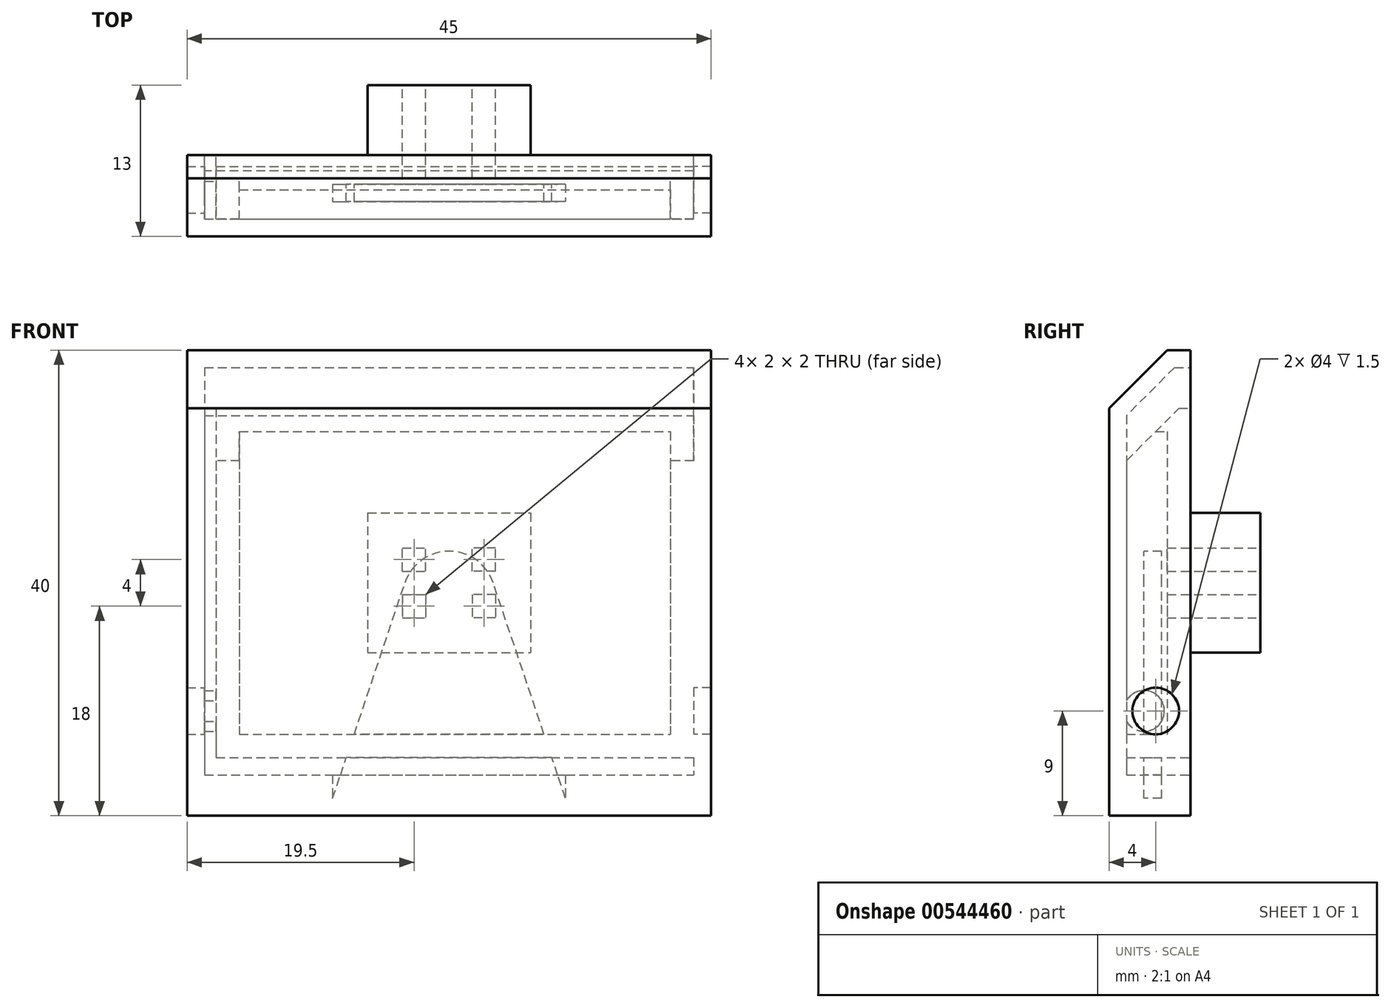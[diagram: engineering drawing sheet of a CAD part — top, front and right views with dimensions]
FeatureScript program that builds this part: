
annotation { "Feature Type Name" : "Feature", "Feature Type Description" : "" }
export const myFeature = defineFeature(function(context is Context, id is Id, definition is map)
    precondition{}
    {
        {
            var Q0;
            Q0=qCreatedBy(makeId("Front.planeOp"),FACE);
            var sketch = newSketch(context, id + "F0", { "sketchPlane" : qUnion([Q0])});
            skLineSegment(sketch, "E0.bottom", {"start": v(-20, 15) * mm, "end": v(21, 15) * mm});
            skLineSegment(sketch, "E0.top", {"start": v(-20, -15) * mm, "end": v(21, -15) * mm});
            skLineSegment(sketch, "E0.left", {"start": v(-20, 15) * mm, "end": v(-20, -15) * mm});
            skLineSegment(sketch, "E0.right", {"start": v(21, 15) * mm, "end": v(21, -15) * mm});
            skSolve(sketch);
        }
        {
            var Q0;
            Q0=makeQuery(id+"F0.imprint","IMPRINT",FACE,{"disambiguationData":[TD([[makeQuery(id+"F0.imprint","IMPRINT",EDGE,{"derivedFrom":sQuery(id+"F0.wireOp",EDGE,"E0.bottom")}),-1.0]])]});
            extrude(context, id + "F1", {"entities" : qUnion([Q0]), "depth" : 6 * mm, "offsetDistance" : 25 * mm});
        }
        {
            var Q0;
            Q0=makeQuery(id+"F1.opExtrude","CAP_FACE",FACE,{"disambiguationData":[OSD([sQuery(id+"F0.wireOp",EDGE,"E0.bottom"),sQuery(id+"F0.wireOp",EDGE,"E0.top"),sQuery(id+"F0.wireOp",EDGE,"E0.left"),sQuery(id+"F0.wireOp",EDGE,"E0.right"),sQuery(id+"F0.wireOp",EDGE,"RBEQEyJk-aGxJ-4fvi-WYVx-bpJPuigMuznj.bottom"),sQuery(id+"F0.wireOp",EDGE,"RBEQEyJk-aGxJ-4fvi-WYVx-bpJPuigMuznj.top"),sQuery(id+"F0.wireOp",EDGE,"RBEQEyJk-aGxJ-4fvi-WYVx-bpJPuigMuznj.left"),sQuery(id+"F0.wireOp",EDGE,"RBEQEyJk-aGxJ-4fvi-WYVx-bpJPuigMuznj.right"),sQuery(id+"F0.wireOp",EDGE,"3556d0db-5f9f-403e-93f9-4f2c554f31b60.MirrorCS"),sQuery(id+"F0.wireOp",EDGE,"3556d0db-5f9f-403e-93f9-4f2c554f31b61.MirrorCS"),sQuery(id+"F0.wireOp",EDGE,"3556d0db-5f9f-403e-93f9-4f2c554f31b62.MirrorCS"),sQuery(id+"F0.wireOp",EDGE,"3556d0db-5f9f-403e-93f9-4f2c554f31b63.MirrorCS"),sQuery(id+"F0.wireOp",EDGE,"c14dda6f-b8be-4261-b637-7746e7f6adf01.MirrorCS"),sQuery(id+"F0.wireOp",EDGE,"c14dda6f-b8be-4261-b637-7746e7f6adf02.MirrorCS"),sQuery(id+"F0.wireOp",EDGE,"c14dda6f-b8be-4261-b637-7746e7f6adf04.MirrorCS"),sQuery(id+"F0.wireOp",EDGE,"c14dda6f-b8be-4261-b637-7746e7f6adf05.MirrorCS"),sQuery(id+"F0.wireOp",EDGE,"c14dda6f-b8be-4261-b637-7746e7f6adf06.MirrorCS"),sQuery(id+"F0.wireOp",EDGE,"c14dda6f-b8be-4261-b637-7746e7f6adf08.MirrorCS"),sQuery(id+"F0.wireOp",EDGE,"c14dda6f-b8be-4261-b637-7746e7f6adf09.MirrorCS"),sQuery(id+"F0.wireOp",EDGE,"c14dda6f-b8be-4261-b637-7746e7f6adf012.MirrorCS")])],"isStart":false});
            shell(context, id + "F2", {"entities" : qUnion([Q0]), "thickness" : 2 * mm});
        }
        {
            var Q0;
            Q0=makeQuery(id+"F0.imprint","IMPRINT",FACE,{"disambiguationData":[TD([[makeQuery(id+"F0.imprint","IMPRINT",EDGE,{"derivedFrom":sQuery(id+"F0.wireOp",EDGE,"E0.bottom")}),-1.0]])]});
            var sketch = newSketch(context, id + "F3", { "sketchPlane" : qUnion([Q0])});
            skLineSegment(sketch, "E1.bottom", {"start": v(-3, -2) * mm, "end": v(3, -2) * mm, "construction": true});
            skLineSegment(sketch, "E1.top", {"start": v(-3, 2) * mm, "end": v(3, 2) * mm, "construction": true});
            skLineSegment(sketch, "E1.left", {"start": v(-3, -2) * mm, "end": v(-3, 2) * mm, "construction": true});
            skLineSegment(sketch, "E1.right", {"start": v(3, -2) * mm, "end": v(3, 2) * mm, "construction": true});
            skPoint(sketch, "E1.middle", {"position": v(0, 0) * mm});
            skLineSegment(sketch, "E2.bottom", {"start": v(-2, -3) * mm, "end": v(-4, -3) * mm});
            skLineSegment(sketch, "E2.top", {"start": v(-2, -1) * mm, "end": v(-4, -1) * mm});
            skLineSegment(sketch, "E2.left", {"start": v(-2, -3) * mm, "end": v(-2, -1) * mm});
            skLineSegment(sketch, "E2.right", {"start": v(-4, -3) * mm, "end": v(-4, -1) * mm});
            skPoint(sketch, "E2.middle", {"position": v(-3, -2) * mm});
            skLineSegment(sketch, "E3.MirrorCS", {"start": v(4, -3) * mm, "end": v(4, -1) * mm});
            skLineSegment(sketch, "E4.MirrorCS", {"start": v(2, -1) * mm, "end": v(4, -1) * mm});
            skLineSegment(sketch, "E5.MirrorCS", {"start": v(2, -3) * mm, "end": v(2, -1) * mm});
            skLineSegment(sketch, "E6.MirrorCS", {"start": v(2, -3) * mm, "end": v(4, -3) * mm});
            skPoint(sketch, "E7.MirrorP", {"position": v(3, -2) * mm});
            skLineSegment(sketch, "E8.MirrorCS", {"start": v(2, 3) * mm, "end": v(2, 1) * mm});
            skLineSegment(sketch, "E9.MirrorCS", {"start": v(2, 1) * mm, "end": v(4, 1) * mm});
            skPoint(sketch, "E10.MirrorP", {"position": v(-3, 2) * mm});
            skLineSegment(sketch, "E11.MirrorCS", {"start": v(-4, 3) * mm, "end": v(-4, 1) * mm});
            skLineSegment(sketch, "E12.MirrorCS", {"start": v(4, 3) * mm, "end": v(4, 1) * mm});
            skLineSegment(sketch, "E13.MirrorCS", {"start": v(2, 3) * mm, "end": v(4, 3) * mm});
            skLineSegment(sketch, "E14.MirrorCS", {"start": v(-2, 3) * mm, "end": v(-2, 1) * mm});
            skLineSegment(sketch, "E15.MirrorCS", {"start": v(-2, 1) * mm, "end": v(-4, 1) * mm});
            skPoint(sketch, "E16.MirrorP", {"position": v(3, 2) * mm});
            skLineSegment(sketch, "E17.MirrorCS", {"start": v(-2, 3) * mm, "end": v(-4, 3) * mm});
            skSolve(sketch);
        }
        {
            var Q0;
            Q0=qSketchRegion(id+"F3",true);
            extrude(context, id + "F4", {"entities" : qUnion([Q0]), "operationType" : NewBodyOperationType.REMOVE, "depth" : 10 * mm, "offsetDistance" : 25 * mm});
        }
        {
            var Q0;
            Q0=makeQuery(id+"F1.opExtrude","SWEPT_FACE",FACE,{"disambiguationData":[OSD([sQuery(id+"F0.wireOp",EDGE,"E0.right")])]});
            var sketch = newSketch(context, id + "F5", { "sketchPlane" : qUnion([Q0])});
            skCircle(sketch, "E18", {"center": v(-4, -11) * mm, "radius": 1.75 * mm});
            skSolve(sketch);
        }
        {
            var Q0;
            Q0=qSketchRegion(id+"F5",true);
            extrude(context, id + "F6", {"entities" : qUnion([Q0]), "operationType" : NewBodyOperationType.ADD, "depth" : 1 * mm, "offsetDistance" : 25 * mm});
        }
        {
            var Q0;
            Q0=makeQuery(id+"F1.opExtrude","SWEPT_FACE",FACE,{"disambiguationData":[OSD([sQuery(id+"F0.wireOp",EDGE,"E0.left")])]});
            var sketch = newSketch(context, id + "F7", { "sketchPlane" : qUnion([Q0])});
            skCircle(sketch, "E19", {"center": v(4, -11) * mm, "radius": 1.75 * mm});
            skSolve(sketch);
        }
        {
            var Q0;
            Q0=qSketchRegion(id+"F7",true);
            extrude(context, id + "F8", {"entities" : qUnion([Q0]), "operationType" : NewBodyOperationType.ADD, "depth" : 1 * mm, "offsetDistance" : 25 * mm});
        }
        {
            var Q0;
            Q0=qCreatedBy(makeId("Front.planeOp"),FACE);
            var sketch = newSketch(context, id + "F9", { "sketchPlane" : qUnion([Q0])});
            skLineSegment(sketch, "E20.bottom", {"start": v(-22.5, 20) * mm, "end": v(22.5, 20) * mm});
            skLineSegment(sketch, "E20.top", {"start": v(-22.5, -20) * mm, "end": v(22.5, -20) * mm});
            skLineSegment(sketch, "E20.left", {"start": v(-22.5, 20) * mm, "end": v(-22.5, -20) * mm});
            skLineSegment(sketch, "E20.right", {"start": v(22.5, 20) * mm, "end": v(22.5, -20) * mm});
            skPoint(sketch, "E20.middle", {"position": v(0, 0) * mm});
            skSolve(sketch);
        }
        {
            var Q0;
            Q0=makeQuery(id+"F9.imprint","IMPRINT",FACE,{"disambiguationData":[TD([[makeQuery(id+"F9.imprint","IMPRINT",EDGE,{"derivedFrom":sQuery(id+"F9.wireOp",EDGE,"E20.bottom")}),-1.0]])]});
            extrude(context, id + "F10", {"entities" : qUnion([Q0]), "depth" : 7 * mm, "offsetDistance" : 25 * mm});
        }
        {
            var Q0;
            Q0=makeQuery(id+"F10.opExtrude","CAP_EDGE",EDGE,{"disambiguationData":[OSD([sQuery(id+"F9.wireOp",EDGE,"E20.bottom")])],"isStart":false});
            chamfer(context, id + "F11", {"entities" : qUnion([Q0]), "width" : 5 * mm, "tangentPropagation" : true});
        }
        {
            var Q0;
            Q0=makeQuery(id+"F10.opExtrude","CAP_FACE",FACE,{"disambiguationData":[OSD([sQuery(id+"F9.wireOp",EDGE,"E20.bottom"),sQuery(id+"F9.wireOp",EDGE,"E20.top"),sQuery(id+"F9.wireOp",EDGE,"E20.left"),sQuery(id+"F9.wireOp",EDGE,"E20.right")])],"isStart":true});
            shell(context, id + "F12", {"entities" : qUnion([Q0]), "thickness" : 1.5 * mm});
        }
        {
            var Q0;
            Q0=makeQuery(id+"F1.opExtrude","CAP_EDGE",EDGE,{"disambiguationData":[OSD([sQuery(id+"F0.wireOp",EDGE,"E0.bottom")])],"isStart":false});
            chamfer(context, id + "F13", {"entities" : qUnion([Q0]), "width" : 5 * mm, "tangentPropagation" : true});
        }
        {
            var Q0;
            Q0=makeQuery(id+"F12.opShell","OFFSET_FACE",FACE,{"disambiguationData":[OSD([sQuery(id+"F9.wireOp",EDGE,"E20.bottom"),sQuery(id+"F9.wireOp",EDGE,"E20.top"),sQuery(id+"F9.wireOp",EDGE,"E20.left"),sQuery(id+"F9.wireOp",EDGE,"E20.right")])]});
            cPlane(context, id + "F14", {"entities" : qUnion([Q0]), "cplaneType" : CPlaneType.OFFSET, "offset" : 1.5 * mm, "width" : 150 * mm, "height" : 150 * mm});
        }
        {
            var Q0;
            Q0=qCreatedBy(id+"F14.planeOp",FACE);
            var sketch = newSketch(context, id + "F15", { "sketchPlane" : qUnion([Q0])});
            skLineSegment(sketch, "E21", {"start": v(21, -18.5) * mm, "end": v(-21, -18.5) * mm});
            skLineSegment(sketch, "E22", {"start": v(-10, -18.5) * mm, "end": v(-3.8, 0) * mm});
            skLineSegment(sketch, "E23.MirrorCS", {"start": v(10, -18.5) * mm, "end": v(3.8, 0) * mm});
            skArc(sketch, "E24", {"start": v(3.8, 0) * mm, "mid": v(0, 2.73) * mm, "end": v(-3.8, 0) * mm});
            skSolve(sketch);
        }
        {
            var Q0;
            {var subQ0=sQuery(id+"F15.wireOp",EDGE,"E22");Q0=makeQuery(id+"F15.imprint","IMPRINT",FACE,{"disambiguationData":[TD([[makeQuery(id+"F15.imprint","IMPRINT",EDGE,{"derivedFrom":subQ0}),-1.0]])]});}
            extrude(context, id + "F16", {"entities" : qUnion([Q0]), "operationType" : NewBodyOperationType.ADD, "depth" : 1.5 * mm});
        }
        {
            var Q0;
            Q0=makeQuery(id+"F12.opShell","OFFSET_FACE",FACE,{"disambiguationData":[OSD([sQuery(id+"F9.wireOp",EDGE,"E20.left")])]});
            var sketch = newSketch(context, id + "F17", { "sketchPlane" : qUnion([Q0])});
            skCircle(sketch, "E25", {"center": v(-3, -11) * mm, "radius": 2 * mm});
            skSolve(sketch);
        }
        {
            var Q0;
            Q0=makeQuery(id+"F17.imprint","IMPRINT",FACE,{"disambiguationData":[TD([[makeQuery(id+"F17.imprint","IMPRINT",EDGE,{"derivedFrom":sQuery(id+"F17.wireOp",EDGE,"E25")}),1.0]])]});
            extrude(context, id + "F18", {"entities" : qUnion([Q0]), "operationType" : NewBodyOperationType.REMOVE, "oppositeDirection" : true, "depth" : 25 * mm});
        }
        {
            var Q0;
            Q0=makeQuery(id+"F12.opShell","OFFSET_FACE",FACE,{"disambiguationData":[OSD([sQuery(id+"F9.wireOp",EDGE,"E20.right")])]});
            var sketch = newSketch(context, id + "F19", { "sketchPlane" : qUnion([Q0])});
            skCircle(sketch, "E26", {"center": v(3, -11) * mm, "radius": 2 * mm});
            skSolve(sketch);
        }
        {
            var Q0;
            Q0=makeQuery(id+"F19.imprint","IMPRINT",FACE,{"disambiguationData":[TD([[makeQuery(id+"F19.imprint","IMPRINT",EDGE,{"derivedFrom":sQuery(id+"F19.wireOp",EDGE,"E26")}),1.0]])]});
            extrude(context, id + "F20", {"entities" : qUnion([Q0]), "operationType" : NewBodyOperationType.REMOVE, "oppositeDirection" : true, "depth" : 25 * mm, "offsetDistance" : 25 * mm});
        }
        {
            var Q0;
            Q0=makeQuery(id+"F12.opShell","OFFSET_FACE",FACE,{"disambiguationData":[OSD([sQuery(id+"F9.wireOp",EDGE,"E20.top")])]});
            var Q1;
            Q1 = qSketchRegion(id + "FXdK867XOb8jO3x_2", true);
            extrude(context, id + "F21", {"entities" : qUnion([Q0, Q1]), "operationType" : NewBodyOperationType.ADD, "depth" : 2 * mm, "offsetDistance" : 25 * mm});
        }
        {
            var Q0;
            Q0=makeQuery(id+"F2.opShell","OFFSET_FACE",FACE,{"disambiguationData":[OSD([sQuery(id+"F0.wireOp",EDGE,"E0.bottom"),sQuery(id+"F0.wireOp",EDGE,"E0.top"),sQuery(id+"F0.wireOp",EDGE,"E0.left"),sQuery(id+"F0.wireOp",EDGE,"E0.right")])]});
            var sketch = newSketch(context, id + "F22", { "sketchPlane" : qUnion([Q0])});
            skLineSegment(sketch, "E27.bottom", {"start": v(-7, 6) * mm, "end": v(7, 6) * mm});
            skLineSegment(sketch, "E27.top", {"start": v(-7, -6) * mm, "end": v(7, -6) * mm});
            skLineSegment(sketch, "E27.left", {"start": v(-7, 6) * mm, "end": v(-7, -6) * mm});
            skLineSegment(sketch, "E27.right", {"start": v(7, 6) * mm, "end": v(7, -6) * mm});
            skPoint(sketch, "E27.middle", {"position": v(0, 0) * mm});
            skSolve(sketch);
        }
        {
            var Q0;
            Q0=makeQuery(id+"F22.imprint","IMPRINT",FACE,{"disambiguationData":[TD([[makeQuery(id+"F22.imprint","IMPRINT",EDGE,{"derivedFrom":sQuery(id+"F22.wireOp",EDGE,"E27.bottom")}),-1.0]])]});
            extrude(context, id + "F23", {"entities" : qUnion([Q0]), "operationType" : NewBodyOperationType.ADD, "oppositeDirection" : true, "depth" : 8 * mm, "offsetDistance" : 25 * mm});
        }
    });
